# Revit family: CRTD-3523
name_source: partatom
category: Lighting Fixtures
units: mm (PartAtom-declared; Revit-internal decimal feet)

## family parameters
Always vertical = Yes
Cut with Voids When Loaded = No
Host = Ceiling
Light Source = Yes
OmniClass Number = 23.80.70.11
OmniClass Title = Luminaries for Internal Lighting
Part Type = Normal
Room Calculation Point = No
Round Connector Dimension = Use Diameter
Shared = No

## types (2) — shared parameters
Color Filter = 16777215
Description = LED Cleanroom Tear Drop Surface
Dimming Lamp Color Temperature Shift = <None>
Housing Finish = Metal - Viscor - White
Lamp = LED
Lens Finish = Acrylic - Viscor - Frosted Round
Manufacturer = CERTOLUX by VISCOR
Model = CRTD-3523
Tilt Angle = 90.00°
Voltage = 120 V

## per-type parameters (varying)
| type | Apparent Load | Assembly Code | Emit from Line Length | Lamp Wattage | Length | Photometric Web File | URL |
| CRTD-3523 48-LED840K52LUNV | 35 VA | D5020200 | 4' - 0" | 35 VA | 4' - 0" | CRTD48-LED840K052LUNV.ies | https://www.viscor.com |
| CRTD-3523 24-LED840K26LUNV | 18 VA |  | 2' - 0" | 18 VA | 2' - 0" | CRTD24-LED840K026LUNV.ies |  |

## geometry (parser evidence)
native form markers: Sweep x2
no freeform markers — native parametric forms only
